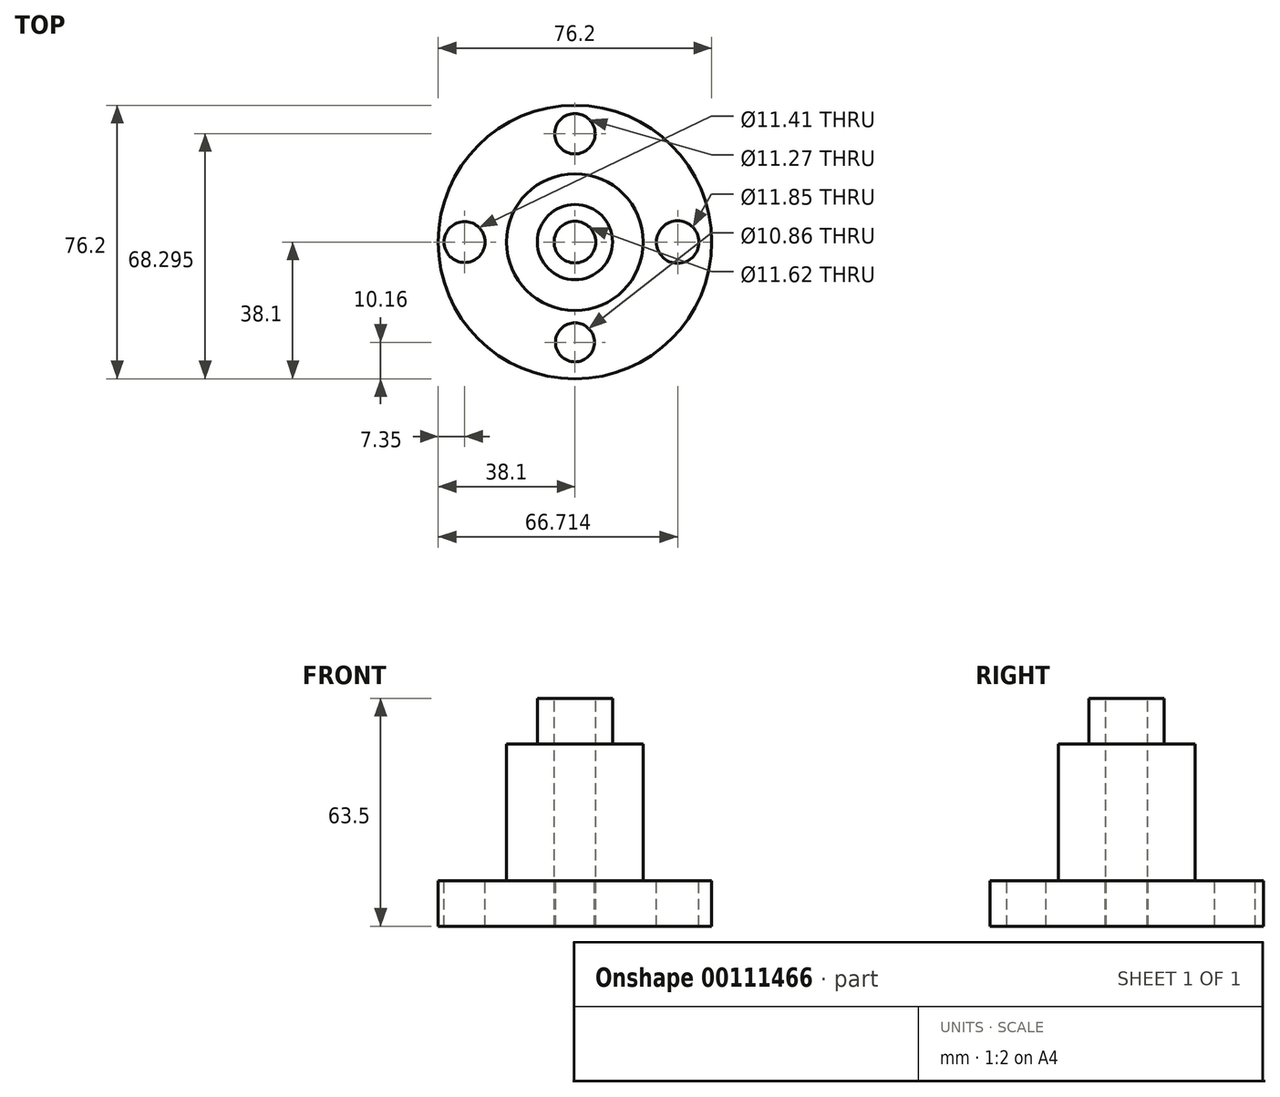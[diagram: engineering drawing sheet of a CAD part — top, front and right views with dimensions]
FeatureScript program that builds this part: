
annotation { "Feature Type Name" : "Feature", "Feature Type Description" : "" }
export const myFeature = defineFeature(function(context is Context, id is Id, definition is map)
    precondition{}
    {
        {
            var Q0;
            Q0=qCreatedBy(makeId("Top.planeOp"),FACE);
            var sketch = newSketch(context, id + "F0", { "sketchPlane" : qUnion([Q0])});
            skCircle(sketch, "E0", {"center": v(0, 0) * mm, "radius": 38.1 * mm});
            skSolve(sketch);
        }
        {
            var Q0;
            Q0 = qSketchRegion(id + "F0", true);
            extrude(context, id + "F1", {"entities" : qUnion([Q0]), "oppositeDirection" : true, "depth" : 12.7 * mm});
        }
        {
            var Q0;
            Q0=makeQuery(id+"F1.opExtrude","CAP_FACE",FACE,{"disambiguationData":[OSD([sQuery(id+"F0.wireOp",EDGE,"E0")])],"isStart":true});
            var sketch = newSketch(context, id + "F2", { "sketchPlane" : qUnion([Q0])});
            skCircle(sketch, "E1", {"center": v(0, 0) * mm, "radius": 19.05 * mm});
            skSolve(sketch);
        }
        {
            var Q0;
            Q0 = qSketchRegion(id + "F2", true);
            extrude(context, id + "F3", {"entities" : qUnion([Q0]), "operationType" : NewBodyOperationType.ADD, "depth" : 38.1 * mm});
        }
        {
            var Q0;
            Q0=makeQuery(id+"F3.opExtrude","CAP_FACE",FACE,{"disambiguationData":[OSD([sQuery(id+"F2.wireOp",EDGE,"E1")])],"isStart":false});
            var sketch = newSketch(context, id + "F4", { "sketchPlane" : qUnion([Q0])});
            skCircle(sketch, "E2", {"center": v(0, 0) * mm, "radius": 10.47 * mm});
            skSolve(sketch);
        }
        {
            var Q0;
            Q0 = qSketchRegion(id + "F4", true);
            extrude(context, id + "F5", {"entities" : qUnion([Q0]), "operationType" : NewBodyOperationType.ADD, "depth" : 12.7 * mm});
        }
        {
            var Q0;
            Q0=makeQuery(id+"F1.opExtrude","CAP_FACE",FACE,{"disambiguationData":[OSD([sQuery(id+"F0.wireOp",EDGE,"E0")])],"isStart":true});
            var sketch = newSketch(context, id + "F6", { "sketchPlane" : qUnion([Q0])});
            skCircle(sketch, "E3", {"center": v(0, -27.94) * mm, "radius": 5.43 * mm});
            skCircle(sketch, "E4", {"center": v(28.61, 0) * mm, "radius": 5.92 * mm});
            skCircle(sketch, "E5", {"center": v(0, 30.2) * mm, "radius": 5.64 * mm});
            skCircle(sketch, "E6", {"center": v(-30.75, 0) * mm, "radius": 5.7 * mm});
            skSolve(sketch);
        }
        {
            var Q0;
            Q0 = qSketchRegion(id + "F6", true);
            extrude(context, id + "F7", {"entities" : qUnion([Q0]), "operationType" : NewBodyOperationType.REMOVE, "endBound" : BoundingType.THROUGH_ALL, "oppositeDirection" : true, "depth" : 13.7 * mm});
        }
        {
            var Q0;
            Q0=makeQuery(id+"F5.opExtrude","CAP_FACE",FACE,{"disambiguationData":[OSD([sQuery(id+"F4.wireOp",EDGE,"E2")])],"isStart":false});
            var sketch = newSketch(context, id + "F8", { "sketchPlane" : qUnion([Q0])});
            skCircle(sketch, "E7", {"center": v(0, 0) * mm, "radius": 5.8 * mm});
            skSolve(sketch);
        }
        {
            var Q0;
            Q0 = qSketchRegion(id + "F8", true);
            extrude(context, id + "F9", {"entities" : qUnion([Q0]), "operationType" : NewBodyOperationType.REMOVE, "endBound" : BoundingType.THROUGH_ALL, "oppositeDirection" : true, "depth" : 25.4 * mm});
        }
    });
